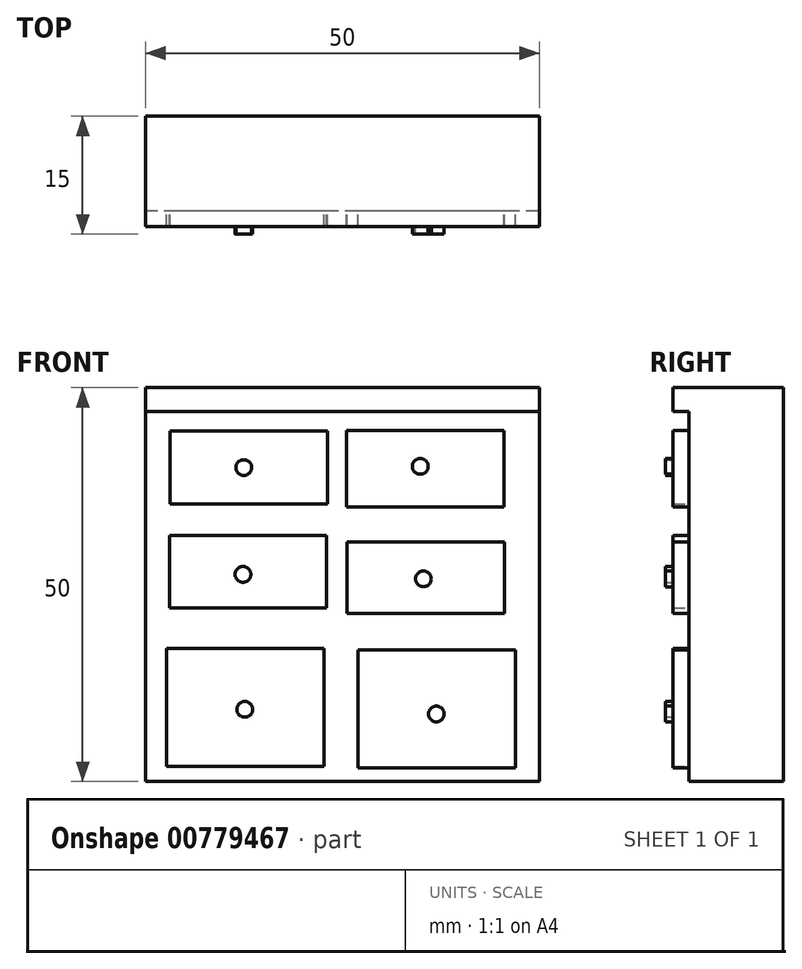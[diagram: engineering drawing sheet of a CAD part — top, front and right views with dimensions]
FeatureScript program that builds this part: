
annotation { "Feature Type Name" : "Feature", "Feature Type Description" : "" }
export const myFeature = defineFeature(function(context is Context, id is Id, definition is map)
    precondition{}
    {
        {
            var Q0;
            Q0=qCreatedBy(makeId("Top.planeOp"),FACE);
            var sketch = newSketch(context, id + "F0", { "sketchPlane" : qUnion([Q0])});
            skLineSegment(sketch, "E0.bottom", {"start": v(0, 0) * mm, "end": v(50, 0) * mm});
            skLineSegment(sketch, "E0.top", {"start": v(0, 12) * mm, "end": v(50, 12) * mm});
            skLineSegment(sketch, "E0.left", {"start": v(0, 0) * mm, "end": v(0, 12) * mm});
            skLineSegment(sketch, "E0.right", {"start": v(50, 0) * mm, "end": v(50, 12) * mm});
            skSolve(sketch);
        }
        {
            var Q0;
            Q0=makeQuery(id+"F0.imprint","IMPRINT",FACE,{"disambiguationData":[TD([[makeQuery(id+"F0.imprint","IMPRINT",EDGE,{"derivedFrom":sQuery(id+"F0.wireOp",EDGE,"E0.bottom")}),1.0]])]});
            extrude(context, id + "F1", {"entities" : qUnion([Q0]), "depth" : 50 * mm, "offsetDistance" : 25 * mm});
        }
        {
            var Q0;
            Q0=makeQuery(id+"F1.opExtrude","SWEPT_FACE",FACE,{"disambiguationData":[OSD([sQuery(id+"F0.wireOp",EDGE,"E0.bottom")])]});
            var sketch = newSketch(context, id + "F2", { "sketchPlane" : qUnion([Q0])});
            skLineSegment(sketch, "E1.bottom", {"start": v(3.08, 44.47) * mm, "end": v(23.08, 44.47) * mm});
            skLineSegment(sketch, "E1.top", {"start": v(3.08, 35.22) * mm, "end": v(23.08, 35.22) * mm});
            skLineSegment(sketch, "E1.left", {"start": v(3.08, 44.47) * mm, "end": v(3.08, 35.22) * mm});
            skLineSegment(sketch, "E1.right", {"start": v(23.08, 44.47) * mm, "end": v(23.08, 35.22) * mm});
            skSolve(sketch);
        }
        {
            var Q0;
            Q0=makeQuery(id+"F2.imprint","IMPRINT",FACE,{"disambiguationData":[TD([[makeQuery(id+"F2.imprint","IMPRINT",EDGE,{"derivedFrom":sQuery(id+"F2.wireOp",EDGE,"E1.bottom")}),1.0]])]});
            var sketch = newSketch(context, id + "F3", { "sketchPlane" : qUnion([Q0])});
            skLineSegment(sketch, "E2.bottom", {"start": v(25.5, 44.6) * mm, "end": v(45.5, 44.6) * mm});
            skLineSegment(sketch, "E2.top", {"start": v(25.5, 34.87) * mm, "end": v(45.5, 34.87) * mm});
            skLineSegment(sketch, "E2.left", {"start": v(25.5, 44.6) * mm, "end": v(25.5, 34.87) * mm});
            skLineSegment(sketch, "E2.right", {"start": v(45.5, 44.6) * mm, "end": v(45.5, 34.87) * mm});
            skSolve(sketch);
        }
        {
            var Q0;
            Q0 = qSketchRegion(id + "F3", true);
            extrude(context, id + "F4", {"entities" : qUnion([Q0]), "operationType" : NewBodyOperationType.ADD, "depth" : 2 * mm, "offsetDistance" : 25 * mm});
        }
        {
            var Q0;
            Q0=makeQuery(id+"F2.imprint","IMPRINT",FACE,{"disambiguationData":[TD([[makeQuery(id+"F2.imprint","IMPRINT",EDGE,{"derivedFrom":sQuery(id+"F2.wireOp",EDGE,"E1.bottom")}),-1.0]])]});
            extrude(context, id + "F5", {"entities" : qUnion([Q0]), "operationType" : NewBodyOperationType.ADD, "depth" : 2 * mm, "offsetDistance" : 25 * mm});
        }
        {
            var Q0;
            Q0=makeQuery(id+"F1.opExtrude","SWEPT_FACE",FACE,{"disambiguationData":[OSD([sQuery(id+"F0.wireOp",EDGE,"E0.bottom")])]});
            var sketch = newSketch(context, id + "F6", { "sketchPlane" : qUnion([Q0])});
            skLineSegment(sketch, "E3.bottom", {"start": v(3, 31.24) * mm, "end": v(22.95, 31.24) * mm});
            skLineSegment(sketch, "E3.top", {"start": v(3, 22.02) * mm, "end": v(22.95, 22.02) * mm});
            skLineSegment(sketch, "E3.left", {"start": v(3, 31.24) * mm, "end": v(3, 22.02) * mm});
            skLineSegment(sketch, "E3.right", {"start": v(22.95, 31.24) * mm, "end": v(22.95, 22.02) * mm});
            skSolve(sketch);
        }
        {
            var Q0;
            Q0 = qSketchRegion(id + "F6", true);
            extrude(context, id + "F7", {"entities" : qUnion([Q0]), "operationType" : NewBodyOperationType.ADD, "depth" : 2 * mm, "offsetDistance" : 25 * mm});
        }
        {
            var Q0;
            Q0=makeQuery(id+"F1.opExtrude","SWEPT_FACE",FACE,{"disambiguationData":[OSD([sQuery(id+"F0.wireOp",EDGE,"E0.bottom")])]});
            var sketch = newSketch(context, id + "F8", { "sketchPlane" : qUnion([Q0])});
            skLineSegment(sketch, "E4.bottom", {"start": v(25.6, 30.4) * mm, "end": v(45.6, 30.4) * mm});
            skLineSegment(sketch, "E4.top", {"start": v(25.6, 21.35) * mm, "end": v(45.6, 21.35) * mm});
            skLineSegment(sketch, "E4.left", {"start": v(25.6, 30.4) * mm, "end": v(25.6, 21.35) * mm});
            skLineSegment(sketch, "E4.right", {"start": v(45.6, 30.4) * mm, "end": v(45.6, 21.35) * mm});
            skSolve(sketch);
        }
        {
            var Q0;
            Q0=makeQuery(id+"F8.imprint","IMPRINT",FACE,{"disambiguationData":[TD([[makeQuery(id+"F8.imprint","IMPRINT",EDGE,{"derivedFrom":sQuery(id+"F8.wireOp",EDGE,"E4.bottom")}),-1.0]])]});
            extrude(context, id + "F9", {"entities" : qUnion([Q0]), "operationType" : NewBodyOperationType.ADD, "depth" : 2 * mm, "offsetDistance" : 25 * mm});
        }
        {
            var Q0;
            Q0=makeQuery(id+"F1.opExtrude","SWEPT_FACE",FACE,{"disambiguationData":[OSD([sQuery(id+"F0.wireOp",EDGE,"E0.bottom")])]});
            var sketch = newSketch(context, id + "F10", { "sketchPlane" : qUnion([Q0])});
            skLineSegment(sketch, "E5.bottom", {"start": v(2.62, 16.89) * mm, "end": v(22.62, 16.89) * mm});
            skLineSegment(sketch, "E5.top", {"start": v(2.62, 1.89) * mm, "end": v(22.62, 1.89) * mm});
            skLineSegment(sketch, "E5.left", {"start": v(2.62, 16.89) * mm, "end": v(2.62, 1.89) * mm});
            skLineSegment(sketch, "E5.right", {"start": v(22.62, 16.89) * mm, "end": v(22.62, 1.89) * mm});
            skSolve(sketch);
        }
        {
            var Q0;
            Q0 = qSketchRegion(id + "F10", true);
            extrude(context, id + "F11", {"entities" : qUnion([Q0]), "operationType" : NewBodyOperationType.ADD, "depth" : 2 * mm, "offsetDistance" : 25 * mm});
        }
        {
            var Q0;
            Q0=makeQuery(id+"F1.opExtrude","SWEPT_FACE",FACE,{"disambiguationData":[OSD([sQuery(id+"F0.wireOp",EDGE,"E0.bottom")])]});
            var sketch = newSketch(context, id + "F12", { "sketchPlane" : qUnion([Q0])});
            skLineSegment(sketch, "E6.bottom", {"start": v(26.94, 16.72) * mm, "end": v(46.94, 16.72) * mm});
            skLineSegment(sketch, "E6.top", {"start": v(26.94, 1.72) * mm, "end": v(46.94, 1.72) * mm});
            skLineSegment(sketch, "E6.left", {"start": v(26.94, 16.72) * mm, "end": v(26.94, 1.72) * mm});
            skLineSegment(sketch, "E6.right", {"start": v(46.94, 16.72) * mm, "end": v(46.94, 1.72) * mm});
            skSolve(sketch);
        }
        {
            var Q0;
            Q0 = qSketchRegion(id + "F12", true);
            extrude(context, id + "F13", {"entities" : qUnion([Q0]), "operationType" : NewBodyOperationType.ADD, "depth" : 2 * mm, "offsetDistance" : 25 * mm});
        }
        {
            var Q0;
            Q0=makeQuery(id+"F5.opExtrude","CAP_FACE",FACE,{"disambiguationData":[OSD([sQuery(id+"F2.wireOp",EDGE,"E1.bottom"),sQuery(id+"F2.wireOp",EDGE,"E1.top"),sQuery(id+"F2.wireOp",EDGE,"E1.left"),sQuery(id+"F2.wireOp",EDGE,"E1.right")])],"isStart":false});
            var sketch = newSketch(context, id + "F14", { "sketchPlane" : qUnion([Q0])});
            skCircle(sketch, "E7", {"center": v(12.45, 39.85) * mm, "radius": 1 * mm});
            skPoint(sketch, "E7.centerSnap0", {"position": v(3.08, 39.85) * mm});
            skSolve(sketch);
        }
        {
            var Q0;
            Q0 = qSketchRegion(id + "F14", true);
            extrude(context, id + "F15", {"entities" : qUnion([Q0]), "operationType" : NewBodyOperationType.ADD, "depth" : 1 * mm, "offsetDistance" : 25 * mm});
        }
        {
            var Q0;
            Q0=makeQuery(id+"F1.opExtrude","SWEPT_FACE",FACE,{"disambiguationData":[OSD([sQuery(id+"F0.wireOp",EDGE,"E0.bottom")])]});
            var sketch = newSketch(context, id + "F16", { "sketchPlane" : qUnion([Q0])});
            skLineSegment(sketch, "E8.bottom", {"start": v(0, 50) * mm, "end": v(50, 50) * mm});
            skLineSegment(sketch, "E8.top", {"start": v(0, 47) * mm, "end": v(50, 47) * mm});
            skLineSegment(sketch, "E8.left", {"start": v(0, 50) * mm, "end": v(0, 47) * mm});
            skLineSegment(sketch, "E8.right", {"start": v(50, 50) * mm, "end": v(50, 47) * mm});
            skSolve(sketch);
        }
        {
            var Q0;
            Q0 = qSketchRegion(id + "F16", true);
            extrude(context, id + "F17", {"entities" : qUnion([Q0]), "operationType" : NewBodyOperationType.ADD, "depth" : 2 * mm, "offsetDistance" : 25 * mm});
        }
        {
            var Q0;
            Q0=makeQuery(id+"F4.opExtrude","CAP_FACE",FACE,{"disambiguationData":[OSD([sQuery(id+"F3.wireOp",EDGE,"E2.bottom"),sQuery(id+"F3.wireOp",EDGE,"E2.top"),sQuery(id+"F3.wireOp",EDGE,"E2.left"),sQuery(id+"F3.wireOp",EDGE,"E2.right")])],"isStart":false});
            var sketch = newSketch(context, id + "F18", { "sketchPlane" : qUnion([Q0])});
            skCircle(sketch, "E9", {"center": v(34.87, 40.02) * mm, "radius": 1 * mm});
            skSolve(sketch);
        }
        {
            var Q0;
            Q0 = qSketchRegion(id + "F18", true);
            extrude(context, id + "F19", {"entities" : qUnion([Q0]), "operationType" : NewBodyOperationType.ADD, "depth" : 1 * mm, "offsetDistance" : 25 * mm});
        }
        {
            var Q0;
            Q0=makeQuery(id+"F7.opExtrude","CAP_FACE",FACE,{"disambiguationData":[OSD([sQuery(id+"F6.wireOp",EDGE,"E3.bottom"),sQuery(id+"F6.wireOp",EDGE,"E3.top"),sQuery(id+"F6.wireOp",EDGE,"E3.left"),sQuery(id+"F6.wireOp",EDGE,"E3.right")])],"isStart":false});
            var sketch = newSketch(context, id + "F20", { "sketchPlane" : qUnion([Q0])});
            skCircle(sketch, "E10", {"center": v(12.35, 26.29) * mm, "radius": 1 * mm});
            skSolve(sketch);
        }
        {
            var Q0;
            Q0 = qSketchRegion(id + "F20", true);
            extrude(context, id + "F21", {"entities" : qUnion([Q0]), "operationType" : NewBodyOperationType.ADD, "depth" : 1 * mm, "offsetDistance" : 25 * mm});
        }
        {
            var Q0;
            Q0=makeQuery(id+"F9.opExtrude","CAP_FACE",FACE,{"disambiguationData":[OSD([sQuery(id+"F8.wireOp",EDGE,"E4.bottom"),sQuery(id+"F8.wireOp",EDGE,"E4.top"),sQuery(id+"F8.wireOp",EDGE,"E4.left"),sQuery(id+"F8.wireOp",EDGE,"E4.right")])],"isStart":false});
            var sketch = newSketch(context, id + "F22", { "sketchPlane" : qUnion([Q0])});
            skCircle(sketch, "E11", {"center": v(35.27, 25.72) * mm, "radius": 1 * mm});
            skSolve(sketch);
        }
        {
            var Q0;
            Q0 = qSketchRegion(id + "F22", true);
            extrude(context, id + "F23", {"entities" : qUnion([Q0]), "operationType" : NewBodyOperationType.ADD, "depth" : 1 * mm, "offsetDistance" : 25 * mm});
        }
        {
            var Q0;
            Q0=makeQuery(id+"F11.opExtrude","CAP_FACE",FACE,{"disambiguationData":[OSD([sQuery(id+"F10.wireOp",EDGE,"E5.bottom"),sQuery(id+"F10.wireOp",EDGE,"E5.top"),sQuery(id+"F10.wireOp",EDGE,"E5.left"),sQuery(id+"F10.wireOp",EDGE,"E5.right")])],"isStart":false});
            var sketch = newSketch(context, id + "F24", { "sketchPlane" : qUnion([Q0])});
            skCircle(sketch, "E12", {"center": v(12.58, 9.15) * mm, "radius": 1 * mm});
            skCircle(sketch, "E13", {"center": v(36.91, 8.55) * mm, "radius": 1 * mm});
            skSolve(sketch);
        }
        {
            var Q0;
            Q0 = qSketchRegion(id + "F24", true);
            extrude(context, id + "F25", {"entities" : qUnion([Q0]), "operationType" : NewBodyOperationType.ADD, "depth" : 1 * mm, "offsetDistance" : 25 * mm});
        }
    });
